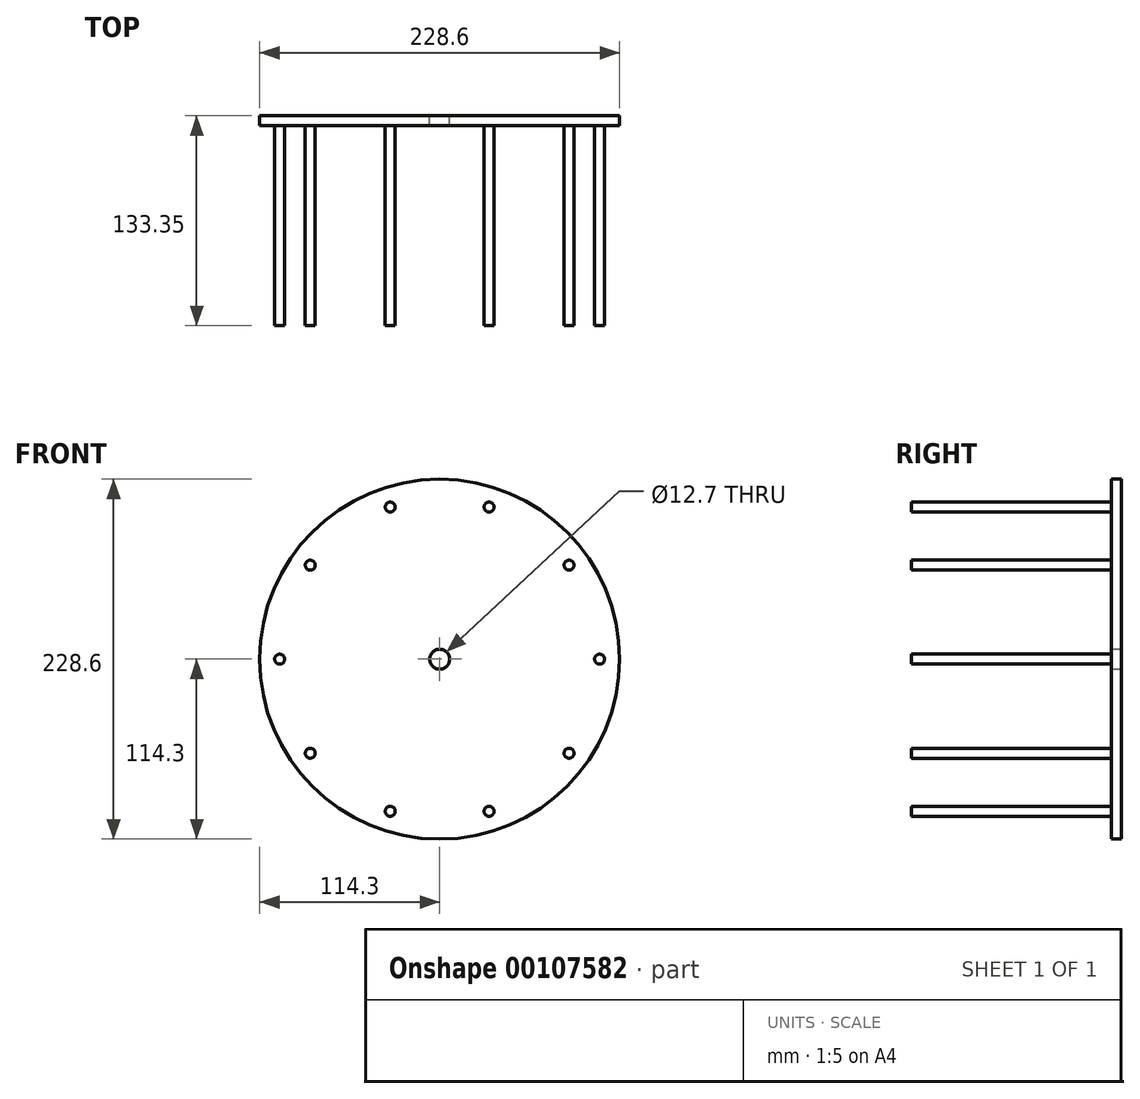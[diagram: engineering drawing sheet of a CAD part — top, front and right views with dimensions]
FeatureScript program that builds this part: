
annotation { "Feature Type Name" : "Feature", "Feature Type Description" : "" }
export const myFeature = defineFeature(function(context is Context, id is Id, definition is map)
    precondition{}
    {
        {
            var Q0;
            Q0=qCreatedBy(makeId("Front.planeOp"),FACE);
            var sketch = newSketch(context, id + "F0", { "sketchPlane" : qUnion([Q0])});
            skCircle(sketch, "E0", {"center": v(0, 0) * mm, "radius": 114.3 * mm});
            skCircle(sketch, "E1", {"center": v(0, 0) * mm, "radius": 6.35 * mm});
            skSolve(sketch);
        }
        {
            var Q0;
            Q0=qSketchRegion(id+"F0",true);
            extrude(context, id + "F1", {"entities" : qUnion([Q0]), "depth" : 6.35 * mm});
        }
        {
            var Q0;
            Q0=makeQuery(id+"F1.opExtrude","CAP_FACE",FACE,{"disambiguationData":[OSD([sQuery(id+"F0.wireOp",EDGE,"E0"),sQuery(id+"F0.wireOp",EDGE,"E1")])],"isStart":false});
            var sketch = newSketch(context, id + "F2", { "sketchPlane" : qUnion([Q0])});
            skCircle(sketch, "E2", {"center": v(0, 0) * mm, "radius": 101.6 * mm, "construction": true});
            skCircle(sketch, "E3", {"center": v(101.6, 0) * mm, "radius": 3.18 * mm});
            skCircle(sketch, "E4.1.0", {"center": v(82.2, 59.72) * mm, "radius": 3.18 * mm});
            skCircle(sketch, "E4.2.0", {"center": v(31.4, 96.63) * mm, "radius": 3.17 * mm});
            skCircle(sketch, "E5.1.3.0", {"center": v(-31.4, 96.63) * mm, "radius": 3.18 * mm});
            skCircle(sketch, "E5.1.4.0", {"center": v(-82.2, 59.72) * mm, "radius": 3.18 * mm});
            skCircle(sketch, "E5.1.5.0", {"center": v(-101.6, 0) * mm, "radius": 3.17 * mm});
            skCircle(sketch, "E5.1.6.0", {"center": v(-82.2, -59.72) * mm, "radius": 3.17 * mm});
            skCircle(sketch, "E5.1.7.0", {"center": v(-31.4, -96.63) * mm, "radius": 3.18 * mm});
            skCircle(sketch, "E5.1.8.0", {"center": v(31.4, -96.63) * mm, "radius": 3.18 * mm});
            skCircle(sketch, "E5.1.9.0", {"center": v(82.2, -59.72) * mm, "radius": 3.18 * mm});
            skSolve(sketch);
        }
        {
            var Q0;
            Q0=qSketchRegion(id+"F2",true);
            extrude(context, id + "F3", {"entities" : qUnion([Q0]), "operationType" : NewBodyOperationType.ADD, "depth" : 127 * mm});
        }
    });
